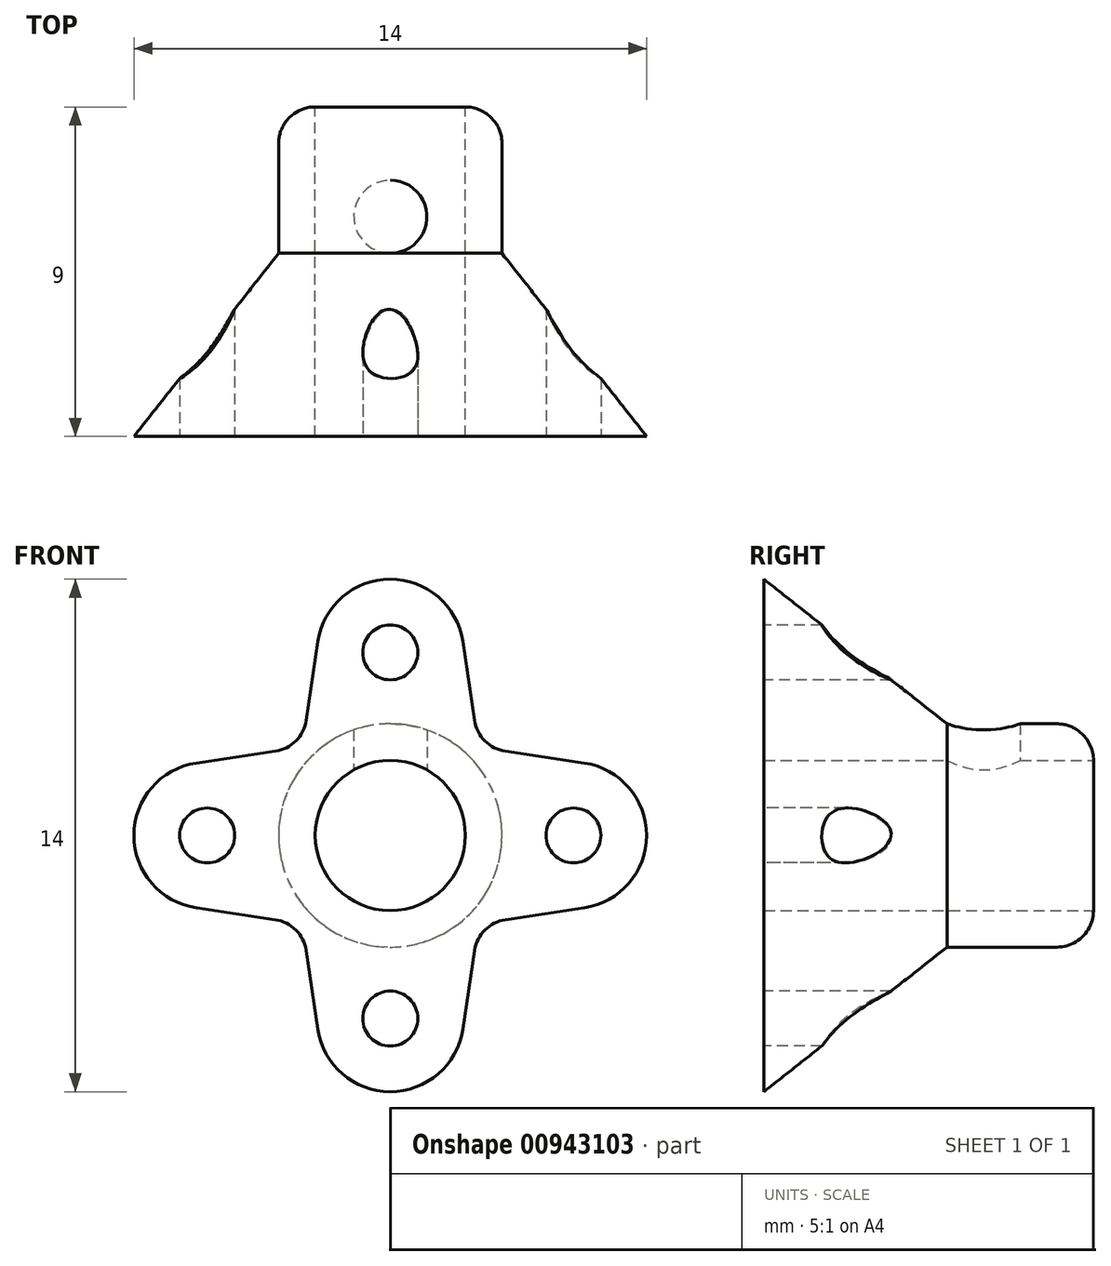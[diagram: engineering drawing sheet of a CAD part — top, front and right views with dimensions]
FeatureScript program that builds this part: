
annotation { "Feature Type Name" : "Feature", "Feature Type Description" : "" }
export const myFeature = defineFeature(function(context is Context, id is Id, definition is map)
    precondition{}
    {
        {
            var Q0;
            Q0=qCreatedBy(makeId("Front.planeOp"),FACE);
            var sketch = newSketch(context, id + "F0", { "sketchPlane" : qUnion([Q0])});
            skCircle(sketch, "E0", {"center": v(0, 0) * mm, "radius": 2.05 * mm});
            skCircle(sketch, "E1", {"center": v(0, 0) * mm, "radius": 3.05 * mm});
            skSolve(sketch);
        }
        {
            var Q0;
            Q0=qSketchRegion(id+"F0",true);
            var Q1;
            Q1=makeQuery(id+"F0.imprint","IMPRINT",FACE,{"disambiguationData":[TD([[makeQuery(id+"F0.imprint","IMPRINT",EDGE,{"derivedFrom":sQuery(id+"F0.wireOp",EDGE,"E0")}),1.0]])]});
            extrude(context, id + "F1", {"entities" : qUnion([Q0, Q1]), "depth" : 4 * mm, "offsetDistance" : 25 * mm});
        }
        {
            var Q0;
            Q0=makeQuery(id+"F1.opExtrude","CAP_FACE",FACE,{"disambiguationData":[OSD([sQuery(id+"F0.wireOp",EDGE,"E0"),sQuery(id+"F0.wireOp",EDGE,"E1")])],"isStart":false});
            cPlane(context, id + "F2", {"entities" : qUnion([Q0]), "cplaneType" : CPlaneType.OFFSET, "offset" : 5 * mm, "width" : 150 * mm, "height" : 150 * mm});
        }
        {
            var Q0;
            Q0=qCreatedBy(id+"F2.planeOp",FACE);
            var sketch = newSketch(context, id + "F3", { "sketchPlane" : qUnion([Q0])});
            skLineSegment(sketch, "E2", {"start": v(-2.3, 3.14) * mm, "end": v(-1.98, 5.3) * mm});
            skLineSegment(sketch, "E3", {"start": v(-3.14, 2.3) * mm, "end": v(-5.3, 1.98) * mm});
            skArc(sketch, "E4", {"start": v(-3.14, 2.3) * mm, "mid": v(-2.58, 2.58) * mm, "end": v(-2.3, 3.14) * mm});
            skArc(sketch, "E5", {"start": v(-1.98, 5.3) * mm, "mid": v(0, 7) * mm, "end": v(1.98, 5.3) * mm});
            skArc(sketch, "E6", {"start": v(-5.3, 1.98) * mm, "mid": v(-7, 0) * mm, "end": v(-5.3, -1.98) * mm});
            skLineSegment(sketch, "E7", {"start": v(-5, 0) * mm, "end": v(0, 5) * mm, "construction": true});
            skLineSegment(sketch, "E8", {"start": v(-3.29, 3.29) * mm, "end": v(0, 0) * mm, "construction": true});
            skLineSegment(sketch, "E9", {"start": v(-5.3, -1.98) * mm, "end": v(-3.14, -2.3) * mm});
            skArc(sketch, "E10", {"start": v(-3.14, -2.3) * mm, "mid": v(-2.58, -2.58) * mm, "end": v(-2.3, -3.14) * mm});
            skLineSegment(sketch, "E11", {"start": v(-2.3, -3.14) * mm, "end": v(-1.98, -5.3) * mm});
            skArc(sketch, "E12", {"start": v(-1.98, -5.3) * mm, "mid": v(0, -7) * mm, "end": v(1.98, -5.3) * mm});
            skLineSegment(sketch, "E13", {"start": v(1.98, -5.3) * mm, "end": v(2.3, -3.14) * mm});
            skArc(sketch, "E14", {"start": v(2.3, -3.14) * mm, "mid": v(2.58, -2.58) * mm, "end": v(3.14, -2.3) * mm});
            skLineSegment(sketch, "E15", {"start": v(3.14, -2.3) * mm, "end": v(5.3, -1.98) * mm});
            skArc(sketch, "E16", {"start": v(5.3, -1.98) * mm, "mid": v(7, 0) * mm, "end": v(5.3, 1.98) * mm});
            skLineSegment(sketch, "E17", {"start": v(5.3, 1.98) * mm, "end": v(3.14, 2.3) * mm});
            skLineSegment(sketch, "E18", {"start": v(1.98, 5.3) * mm, "end": v(2.3, 3.14) * mm});
            skArc(sketch, "E19", {"start": v(2.3, 3.14) * mm, "mid": v(2.58, 2.58) * mm, "end": v(3.14, 2.3) * mm});
            skCircle(sketch, "E20", {"center": v(-5, 0) * mm, "radius": 0.75 * mm, "construction": true});
            skCircle(sketch, "E21", {"center": v(0, 5) * mm, "radius": 0.75 * mm, "construction": true});
            skCircle(sketch, "E22", {"center": v(5, 0) * mm, "radius": 0.75 * mm, "construction": true});
            skCircle(sketch, "E23", {"center": v(0, -5) * mm, "radius": 0.75 * mm, "construction": true});
            skSolve(sketch);
        }
        {
            var Q1;
            Q1=makeQuery(id+"F3.imprint","IMPRINT",FACE,{"disambiguationData":[TD([[makeQuery(id+"F3.imprint","IMPRINT",EDGE,{"derivedFrom":sQuery(id+"F3.wireOp",EDGE,"E2")}),-1.0]])]});
            var Q2;
            Q2=makeQuery(id+"F1.opExtrude","CAP_FACE",FACE,{"disambiguationData":[OSD([sQuery(id+"F0.wireOp",EDGE,"E1")])],"isStart":false});
            loft(context, id + "F4", {"operationType" : NewBodyOperationType.ADD, "sheetProfilesArray" : [{ "sheetProfileEntities" : qUnion([Q1]) }, { "sheetProfileEntities" : qUnion([Q2]) }]});
        }
        {
            var Q0;
            Q0=sQuery(id+"F3.wireOp",VERTEX,"E16.center");
            var Q1;
            Q1=sQuery(id+"F3.wireOp",VERTEX,"E12.center");
            var Q2;
            Q2=sQuery(id+"F3.wireOp",VERTEX,"E7.start");
            var Q3;
            Q3=sQuery(id+"F3.wireOp",VERTEX,"E7.end");
            var Q4;
            Q4=makeQuery(id+"F1.opExtrude","SWEPT_BODY",BODY,{"disambiguationData":[OSD([sQuery(id+"F0.wireOp",EDGE,"E1")])]});
            hole(context, id + "F5", {"style" : HoleStyle.SIMPLE, "endStyle" : HoleEndStyle.THROUGH, "holeDiameter" : 1.5 * mm, "majorDiameter" : 5 * mm, "isTappedThrough" : true, "tappedDepth" : 12 * mm, "tapClearance" : 3, "locations" : qUnion([Q0, Q1, Q2, Q3]), "scope" : qUnion([Q4])});
        }
        {
            var Q0;
            Q0=makeQuery(id+"F0.imprint","IMPRINT",FACE,{"disambiguationData":[TD([[makeQuery(id+"F0.imprint","IMPRINT",EDGE,{"derivedFrom":sQuery(id+"F0.wireOp",EDGE,"E0")}),1.0]])]});
            extrude(context, id + "F6", {"entities" : qUnion([Q0]), "operationType" : NewBodyOperationType.REMOVE, "depth" : 25 * mm, "offsetDistance" : 25 * mm});
        }
        {
            var Q0;
            Q0=qCreatedBy(makeId("Top.planeOp"),FACE);
            var sketch = newSketch(context, id + "F7", { "sketchPlane" : qUnion([Q0])});
            skPoint(sketch, "E24", {"position": v(0, -3) * mm});
            skSolve(sketch);
        }
        {
            var Q0;
            Q0=sQuery(id+"F7.wireOp",VERTEX,"E24");
            var Q1;
            Q1=makeQuery(id+"F1.opExtrude","SWEPT_BODY",BODY,{"disambiguationData":[OSD([sQuery(id+"F0.wireOp",EDGE,"E1")])]});
            hole(context, id + "F8", {"style" : HoleStyle.SIMPLE, "endStyle" : HoleEndStyle.THROUGH, "oppositeDirection" : true, "holeDiameter" : 2 * mm, "majorDiameter" : 5 * mm, "isTappedThrough" : true, "tappedDepth" : 12 * mm, "tapClearance" : 3, "locations" : qUnion([Q0]), "scope" : qUnion([Q1])});
        }
        {
            var Q0;
            Q0=makeQuery(id+"F1.opExtrude","CAP_EDGE",EDGE,{"disambiguationData":[OSD([sQuery(id+"F0.wireOp",EDGE,"E1")])],"isStart":true});
            fillet(context, id + "F9", {"entities" : qUnion([Q0]), "radius" : 1 * mm, "tangentPropagation" : true, "allowEdgeOverflow" : false});
        }
    });
